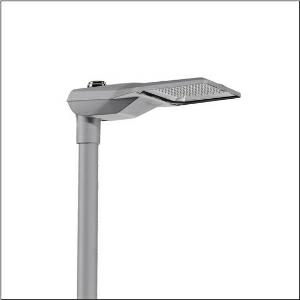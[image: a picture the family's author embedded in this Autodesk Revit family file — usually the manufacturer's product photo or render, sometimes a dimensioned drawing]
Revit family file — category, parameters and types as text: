
# Revit family: streetlight_sl_21_midi___st0_5a_5xe7b37n08nb_a99d
name_source: partatom
category: Lighting Fixtures
units: mm (PartAtom-declared; Revit-internal decimal feet)

## family parameters
Cut with Voids When Loaded = No
Host = Face
Light Source = No
Part Type = Normal
Room Calculation Point = No
Round Connector Dimension = Use Diameter
Shared = No

## types (1)
- --- (1 x LED, 22700 lm, 151.2 W, 3000K)
    Apparent Load = 151 VA
    CIE Flux Codes = 43 76 97 100 100
    Color Rendering = 70
    Color Temperature = 3000K
    Default Elevation = 1800 mm
    Description = Streetlight SL 21 midi, mast luminaire, primary light control with lens, of PMMA, primary optical cover: cover, of toughened safety glass, transparent, light distribution: ST0.5a, light emission: direct distribution, primary light characteristic: asymmetric, installation type: side-entry, LED, 3G 2.5mm², High Power LED, rated luminous flux: 22.700lm, luminous efficacy: 150lm/W, light colour: 730, colour temperature: 3000K, control gear: NEMA (7pin), control: overheat protection, pre-setting: linear dimming characteristic, constant luminous flux control, time-dependent luminous flux control, flexible luminous flux parameterisation, mains connection: 220..240V, AC, 50/60Hz, connection cable pre-assembled, cable length: 12,5m, wiring characteristics: H05VV-F, start of lifetime: 151W, end of service life: 157W, reduction: 70W, luminaire housing, of diecast aluminium (EN AC-44300), powder-coated, SITECO metallic grey (DB 702S), corrosivity category C5 high according to DIN EN ISO 12944, multi-level sealing system, sealing non-destructively replaceable, inclination adjustable: 0°, 5°, 10°, 15°, length: 644mm, width: 335mm, height: 110mm, spigot size: 42mm (side-entry), mounting height: 4..8m, protection rating (complete): IP66, insulation class (complete): insulation class I (protective earthing), certification: CE, ENEC, ENEC+, VDE, impact resistance: IK10, permissible operating ambient temperature for outdoor applications: -40..+50°C, standard-compliant lighting for roads and squares, packaging unit: 1 piece

Light Distribution: ST0.5a
    Height = 111 mm
    Lamp = 1 x LED
    Lamp Light Flux = 22700 lm
    Lamp Power = 151.2 W
    Lamp count = 1
    Length = 644 mm
    Luminous efficacy = 150 lm/W
    Manufacturer = Siteco
    ModVariant = No
    Model = 5XE7B37N08NB
    Number of Poles = 1
    OnlyDefault = Yes
    Power Factor = 1
    Product Name = Streetlight SL 21 midi | ST0.5a
    Product group = mast luminaire | pylon top
    ProductGroupID = 6100
    Protection Class = Protection class I
    Protection Degree = IP 66
    RLX_Detail_Level = 1
    RLX_Emergency_Light_Flux = 0 lm
    RLX_Emergency_Type = 0
    RLX_Emergency_Type_DB = No
    RlxData = <blob elided: 37765 chars, md5=83c173e3>
    Socket = socket
    Standby Power = 0 W
    System Light Flux = 22700 lm
    System Power = 151 W
    Type Comments = factory setting: luminous flux: 100 % | dim-lin: 254 | 802 mA
    Type Image = l_1294377.jpg
    URL = http://relux.com
    VarID = @adj_136187
    Voltage = 0 V
    Weight = 0.00 kg
    Width = 336 mm

## geometry (parser evidence)
native form markers: Blend x4, Sweep x11
no freeform markers — native parametric forms only
